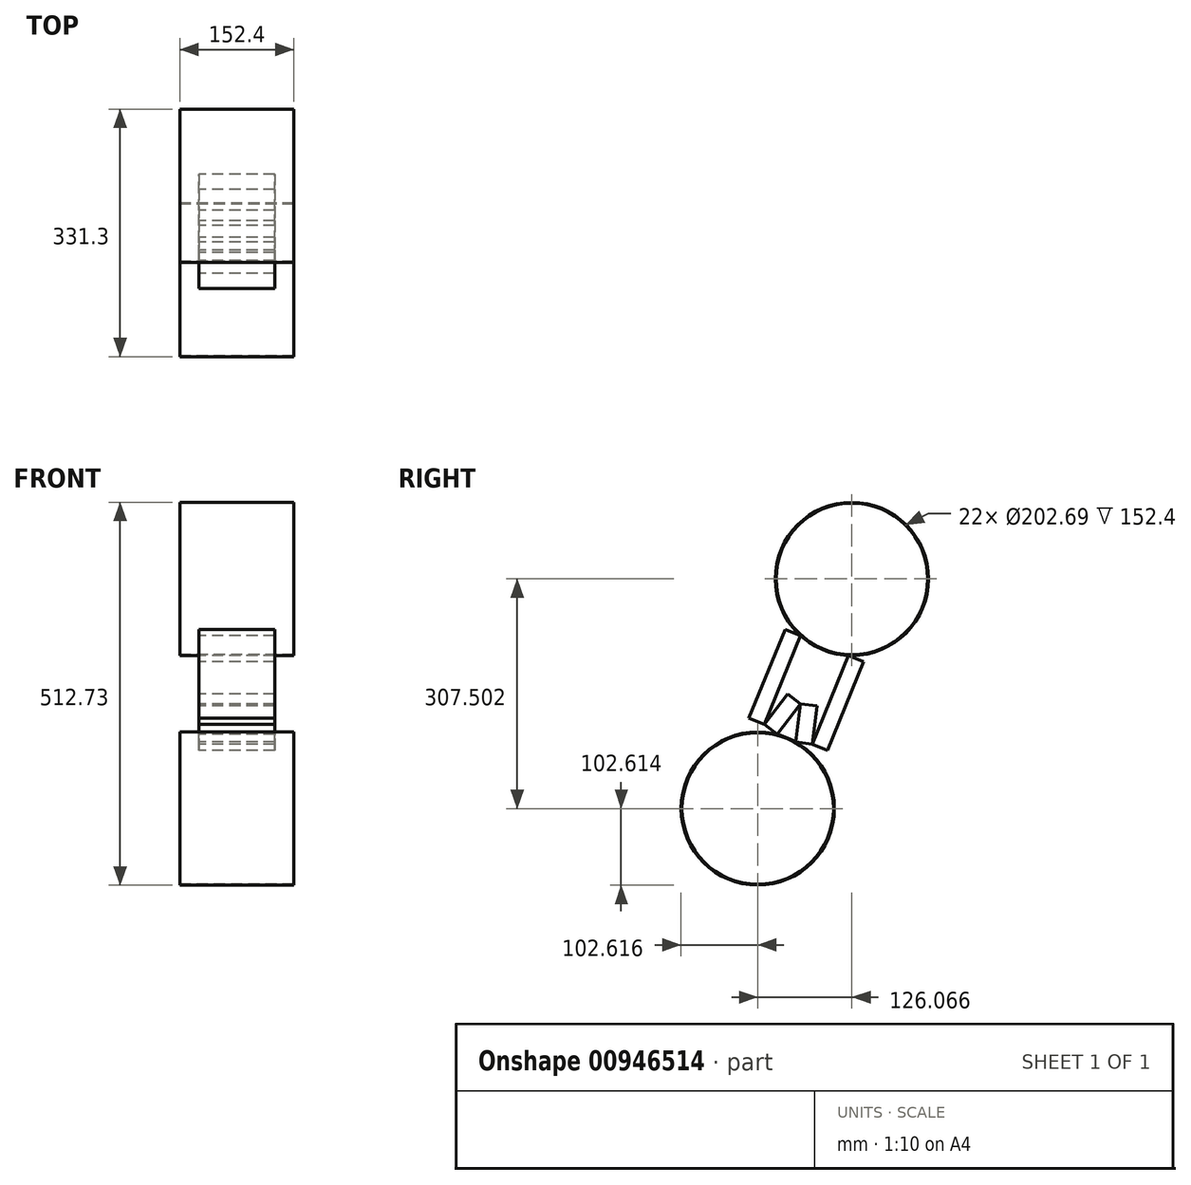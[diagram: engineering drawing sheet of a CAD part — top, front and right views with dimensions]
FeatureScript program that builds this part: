
annotation { "Feature Type Name" : "Feature", "Feature Type Description" : "" }
export const myFeature = defineFeature(function(context is Context, id is Id, definition is map)
    precondition{}
    {
        {
            var Q0;
            Q0=qCreatedBy(makeId("Right.planeOp"),FACE);
            var sketch = newSketch(context, id + "F0", { "sketchPlane" : qUnion([Q0])});
            skLineSegment(sketch, "E0", {"start": v(-365.94, 110.3) * mm, "end": v(-386.38, 118.68) * mm});
            skLineSegment(sketch, "E1", {"start": v(-386.38, 118.68) * mm, "end": v(-435.04, 0) * mm});
            skLineSegment(sketch, "E2", {"start": v(-435.04, 0) * mm, "end": v(-414.6, -8.38) * mm});
            skLineSegment(sketch, "E3", {"start": v(-414.6, -8.38) * mm, "end": v(-365.94, 110.3) * mm});
            skLineSegment(sketch, "E4", {"start": v(-450.46, 144.95) * mm, "end": v(-470.9, 153.33) * mm});
            skLineSegment(sketch, "E5", {"start": v(-470.9, 153.33) * mm, "end": v(-519.56, 34.65) * mm});
            skLineSegment(sketch, "E6", {"start": v(-519.56, 34.65) * mm, "end": v(-499.11, 26.27) * mm});
            skLineSegment(sketch, "E7", {"start": v(-499.11, 26.27) * mm, "end": v(-450.46, 144.95) * mm});
            skLineSegment(sketch, "E8", {"start": v(-428.53, 50.9) * mm, "end": v(-450.45, 53.7) * mm});
            skLineSegment(sketch, "E9", {"start": v(-450.45, 53.7) * mm, "end": v(-456.96, 2.8) * mm});
            skLineSegment(sketch, "E10", {"start": v(-456.96, 2.8) * mm, "end": v(-435.04, 0) * mm});
            skLineSegment(sketch, "E11", {"start": v(-435.04, 0) * mm, "end": v(-428.53, 50.9) * mm});
            skLineSegment(sketch, "E12", {"start": v(-450.45, 53.7) * mm, "end": v(-468.03, 67.09) * mm});
            skLineSegment(sketch, "E13", {"start": v(-468.03, 67.09) * mm, "end": v(-499.11, 26.27) * mm});
            skLineSegment(sketch, "E14", {"start": v(-499.11, 26.27) * mm, "end": v(-481.53, 12.88) * mm});
            skLineSegment(sketch, "E15", {"start": v(-481.53, 12.88) * mm, "end": v(-450.45, 53.7) * mm});
            skCircle(sketch, "E16", {"center": v(-507.84, -86.3) * mm, "radius": 102.62 * mm});
            skCircle(sketch, "E17", {"center": v(-381.78, 221.2) * mm, "radius": 102.62 * mm});
            skCircle(sketch, "E18.0", {"center": v(-507.84, -86.3) * mm, "radius": 101.35 * mm});
            skCircle(sketch, "E19.0", {"center": v(-381.78, 221.2) * mm, "radius": 101.35 * mm});
            skSolve(sketch);
        }
        {
            var Q0;
            Q0=makeQuery(id+"F0.imprint","IMPRINT",FACE,{"disambiguationData":[TD([[makeQuery(id+"F0.imprint","IMPRINT",EDGE,{"derivedFrom":sQuery(id+"F0.wireOp",EDGE,"E19.0")}),-1.0]])]});
            var Q1;
            Q1=makeQuery(id+"F0.imprint","IMPRINT",FACE,{"disambiguationData":[TD([[makeQuery(id+"F0.imprint","IMPRINT",EDGE,{"derivedFrom":sQuery(id+"F0.wireOp",EDGE,"E18.0")}),-1.0]])]});
            extrude(context, id + "F1", {"entities" : qUnion([Q0, Q1]), "endBound" : BoundingType.SYMMETRIC, "depth" : 152.4 * mm, "offsetDistance" : 25.4 * mm});
        }
        {
            var Q0;
            Q0=makeQuery(id+"F0.imprint","IMPRINT",FACE,{"disambiguationData":[TD([[makeQuery(id+"F0.imprint","IMPRINT",EDGE,{"derivedFrom":sQuery(id+"F0.wireOp",EDGE,"E4")}),1.0]])]});
            var Q1;
            Q1=makeQuery(id+"F0.imprint","IMPRINT",FACE,{"disambiguationData":[TD([[makeQuery(id+"F0.imprint","IMPRINT",EDGE,{"derivedFrom":sQuery(id+"F0.wireOp",EDGE,"E12")}),1.0]])]});
            var Q2;
            Q2=makeQuery(id+"F0.imprint","IMPRINT",FACE,{"disambiguationData":[TD([[makeQuery(id+"F0.imprint","IMPRINT",EDGE,{"derivedFrom":sQuery(id+"F0.wireOp",EDGE,"E8")}),1.0]])]});
            var Q3;
            Q3=makeQuery(id+"F0.imprint","IMPRINT",FACE,{"disambiguationData":[TD([[makeQuery(id+"F0.imprint","IMPRINT",EDGE,{"derivedFrom":sQuery(id+"F0.wireOp",EDGE,"E0")}),1.0]])]});
            extrude(context, id + "F2", {"entities" : qUnion([Q0, Q1, Q2, Q3]), "endBound" : BoundingType.SYMMETRIC, "depth" : 101.6 * mm, "offsetDistance" : 25.4 * mm});
        }
    });
